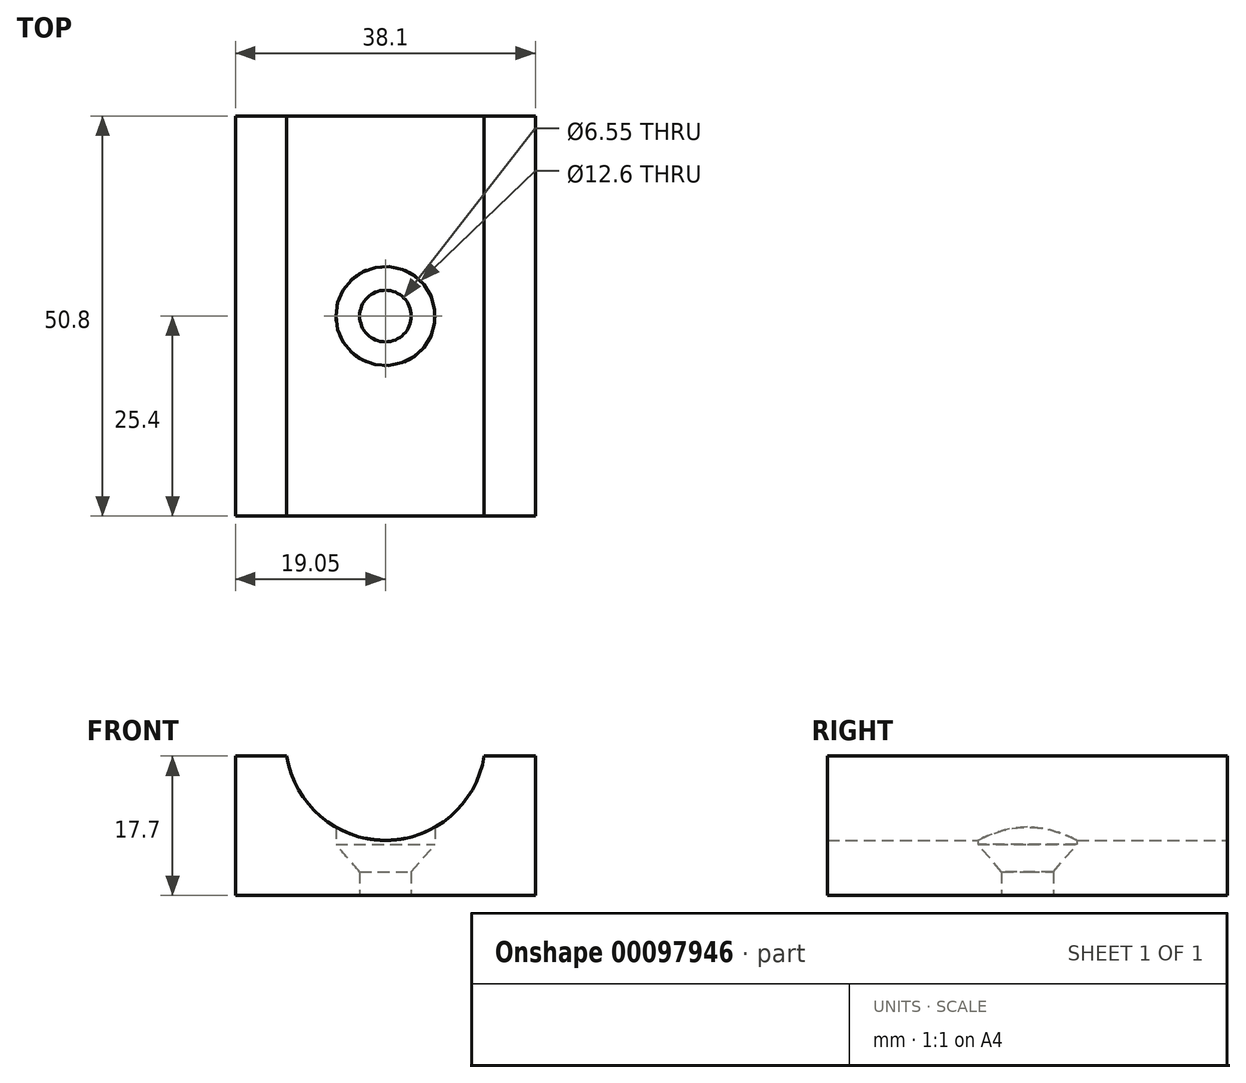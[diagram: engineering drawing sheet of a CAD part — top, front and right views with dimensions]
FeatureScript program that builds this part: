
annotation { "Feature Type Name" : "Feature", "Feature Type Description" : "" }
export const myFeature = defineFeature(function(context is Context, id is Id, definition is map)
    precondition{}
    {
        {
            var Q0;
            Q0=qCreatedBy(makeId("Front.planeOp"),FACE);
            var sketch = newSketch(context, id + "F0", { "sketchPlane" : qUnion([Q0])});
            skLineSegment(sketch, "E0", {"start": v(-19.05, 0) * mm, "end": v(19.05, 0) * mm});
            skLineSegment(sketch, "E1", {"start": v(-19.05, 0) * mm, "end": v(-19.05, 17.7) * mm});
            skLineSegment(sketch, "E2", {"start": v(-19.05, 17.7) * mm, "end": v(-12.54, 17.7) * mm});
            skLineSegment(sketch, "E3", {"start": v(19.05, 0) * mm, "end": v(19.05, 17.7) * mm});
            skLineSegment(sketch, "E4", {"start": v(19.05, 17.7) * mm, "end": v(12.54, 17.7) * mm});
            skArc(sketch, "E5", {"start": v(-12.54, 17.7) * mm, "mid": v(0, 7) * mm, "end": v(12.54, 17.7) * mm});
            skLineSegment(sketch, "E6", {"start": v(-12.54, 17.7) * mm, "end": v(12.54, 17.7) * mm, "construction": true});
            skSolve(sketch);
        }
        {
            var Q0;
            Q0=qCreatedBy(makeId("Front.planeOp"),FACE);
            var sketch = newSketch(context, id + "F1", { "sketchPlane" : qUnion([Q0])});
            skArc(sketch, "E7.0", {"start": v(-12.54, 17.7) * mm, "mid": v(0, 7) * mm, "end": v(12.54, 17.7) * mm, "construction": true});
            skLineSegment(sketch, "E8.bottom", {"start": v(-6.3, 7) * mm, "end": v(6.3, 7) * mm, "construction": true});
            skLineSegment(sketch, "E8.top", {"start": v(-6.3, 17.18) * mm, "end": v(6.3, 17.18) * mm});
            skLineSegment(sketch, "E8.left", {"start": v(-6.3, 7) * mm, "end": v(-6.3, 17.18) * mm});
            skLineSegment(sketch, "E8.right", {"start": v(6.3, 7) * mm, "end": v(6.3, 17.18) * mm});
            skLineSegment(sketch, "E9.bottom", {"start": v(-3.27, 0) * mm, "end": v(3.27, 0) * mm});
            skLineSegment(sketch, "E9.top", {"start": v(-3.28, 3) * mm, "end": v(3.28, 3) * mm, "construction": true});
            skLineSegment(sketch, "E9.left", {"start": v(-3.27, 0) * mm, "end": v(-3.28, 3) * mm});
            skLineSegment(sketch, "E9.right", {"start": v(3.28, 0) * mm, "end": v(3.28, 3) * mm});
            skLineSegment(sketch, "E10", {"start": v(-3.28, 3) * mm, "end": v(-6.3, 6.48) * mm});
            skLineSegment(sketch, "E11", {"start": v(3.27, 3) * mm, "end": v(6.3, 6.48) * mm});
            skLineSegment(sketch, "E12", {"start": v(-6.3, 7) * mm, "end": v(-6.3, 6.48) * mm});
            skLineSegment(sketch, "E13", {"start": v(6.3, 7) * mm, "end": v(6.3, 6.48) * mm});
            skLineSegment(sketch, "E14", {"start": v(0, 7) * mm, "end": v(0, 3) * mm, "construction": true});
            skLineSegment(sketch, "E15", {"start": v(0, 17.18) * mm, "end": v(0, 0) * mm});
            skSolve(sketch);
        }
        {
            var Q0;
            Q0 = qSketchRegion(id + "F0", true);
            extrude(context, id + "F2", {"entities" : qUnion([Q0]), "endBound" : BoundingType.SYMMETRIC, "depth" : 50.8 * mm});
        }
        {
            var Q0;
            {var subQ3=sQuery(id+"F1.wireOp",EDGE,"E8.left");Q0=makeQuery(id+"F1.imprint","IMPRINT",FACE,{"disambiguationData":[TD([[makeQuery(id+"F1.imprint","IMPRINT",EDGE,{"derivedFrom":subQ3}),-1.0]])]});}
            var Q1;
            Q1=sQuery(id+"F1.wireOp",EDGE,"E15");
            revolve(context, id + "F3", {"operationType" : NewBodyOperationType.REMOVE, "entities" : qUnion([Q0]), "axis" : qUnion([Q1]), "revolveType" : RevolveType.FULL, "oppositeDirection" : true});
        }
    });
